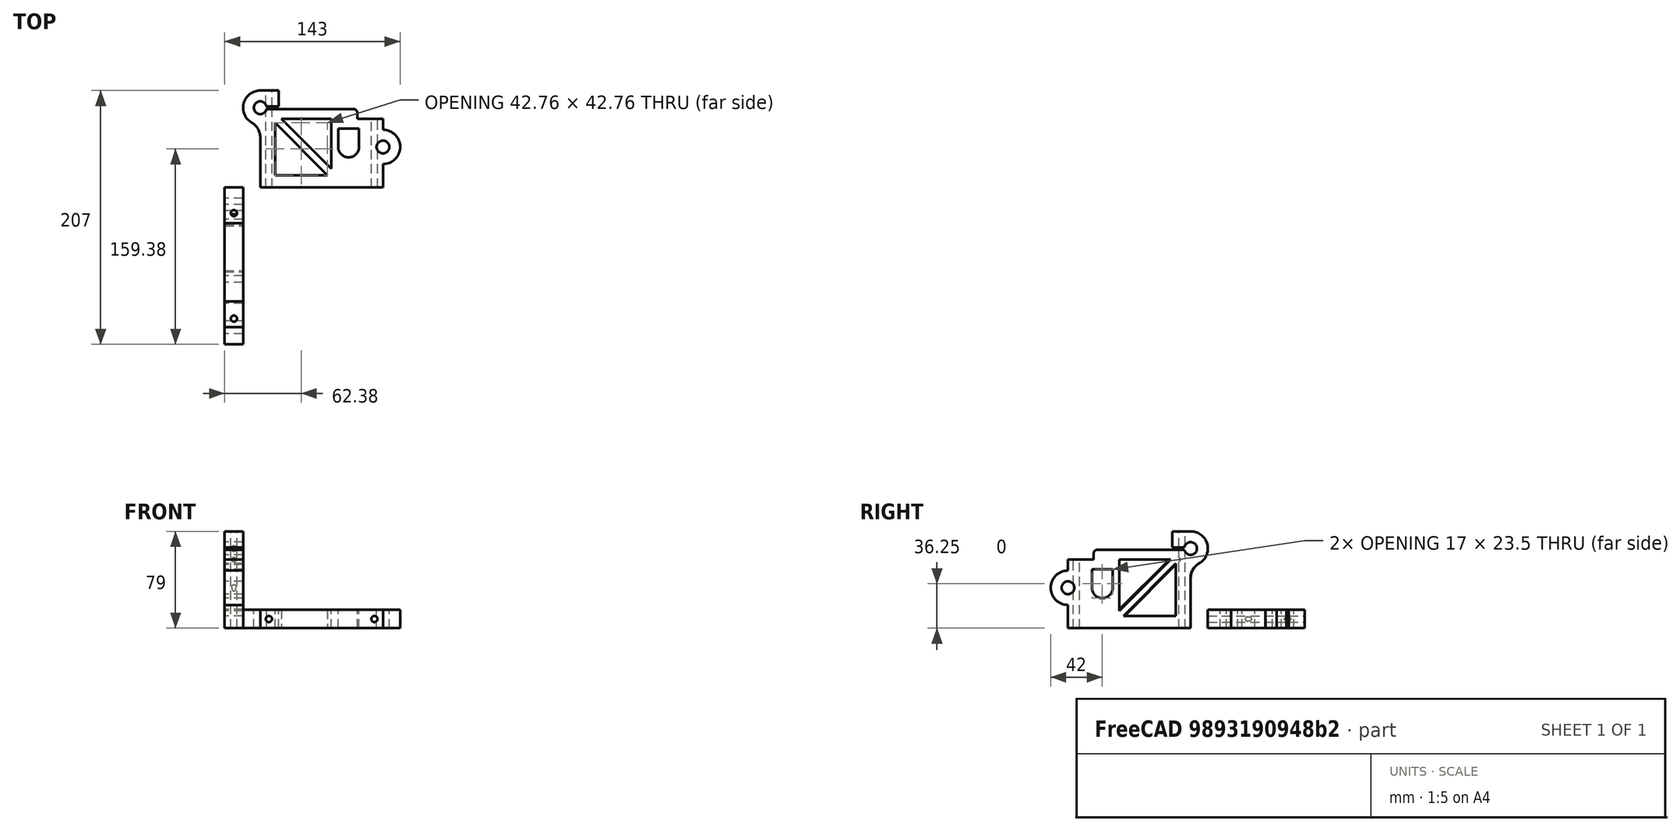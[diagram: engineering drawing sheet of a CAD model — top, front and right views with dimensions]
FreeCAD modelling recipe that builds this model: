
FCSTD DOCUMENT  (FreeCAD 0.15R4666 (Git))
Label: x_right_holder_B
License: All rights reserved
LicenseURL: http://en.wikipedia.org/wiki/All_rights_reserved
objects: Part::Box×7, Part::Cylinder×7, Part::MultiFuse×5, Part::Cut×5, Part::Feature×3, Part::Fillet×2, Mesh::Feature×1
note: 29 computed .brp shape members not serialized (recipe doc carries the construction recipe); baked Part::Feature solids carry a one-line shape summary decoded from their .brp

FEATURE [Part::Box] Box  label="Cubo"
  Height = 15
  Length = 100
  Placement = pos=(14,0,0) rot=(0,0,1;0rad)
  Width = 56
FEATURE [Part::Box] Box001  label="Cubo001"
  Height = 15
  Length = 15
  Placement = pos=(14,56,0) rot=(0,0,1;0rad)
  Width = 23
FEATURE [Part::Box] Box002  label="Cubo002"
  Height = 15
  Length = 64
  Placement = pos=(29,56,0) rot=(0,0,1;0rad)
  Width = 8
FEATURE [Part::Cylinder] Cylinder  label="Cilindro"
  Angle = 360
  Height = 15
  Placement = pos=(14,65,0) rot=(0,0,1;0rad)
  Radius = 14
FEATURE [Part::Cylinder] Cylinder001  label="Cilindro001"
  Angle = 360
  Height = 15
  Placement = pos=(114,33,0) rot=(0,0,1;0rad)
  Radius = 14
FEATURE [Part::Box] Box004  label="Cubo004"
  Height = 15
  Length = 46
  Placement = pos=(26,10,0) rot=(0,0,1;0rad)
  Width = 46
FEATURE [Part::Cylinder] Cylinder002  label="Cilindro002"
  Angle = 360
  Height = 17
  Placement = pos=(14,65,-1) rot=(0,0,1;0rad)
  Radius = 5.2
FEATURE [Part::Cylinder] Cylinder003  label="Cilindro003"
  Angle = 360
  Height = 17
  Placement = pos=(114,33,-1) rot=(0,0,1;0rad)
  Radius = 5.2
FEATURE [Part::MultiFuse] Fusion001  label="rod_holes"
  Shapes = -> [Cylinder002,Cylinder003]
FEATURE [Part::Box] Box006  label="Cubo006"
  Height = 15
  Length = 17
  Placement = pos=(77.5,33,0) rot=(0,0,1;0rad)
  Width = 15
FEATURE [Part::Cylinder] Cylinder004  label="Cilindro004"
  Angle = 360
  Height = 15
  Placement = pos=(86,33,0) rot=(0,0,1;0rad)
  Radius = 8.5
FEATURE [Part::MultiFuse] Fusion002  label="threaded_rod_hole"
  Shapes = -> [Box006,Cylinder004]
FEATURE [Part::Box] Box007  label="offset_hole"
  Height = 17
  Length = 12
  Placement = pos=(18,64,-1) rot=(0,0,1;0rad)
  Width = 2
FEATURE [Part::Cylinder] Cylinder005  label="Cilindro005"
  Angle = 360
  Height = 81
  Placement = pos=(21,-1,7.5) rot=(-1,0,0;1.5708rad)
  Radius = 2.5
FEATURE [Part::Cylinder] Cylinder006  label="Cilindro006"
  Angle = 360
  Height = 58
  Placement = pos=(107,-1,7.5) rot=(-1,0,0;1.5708rad)
  Radius = 2.5
FEATURE [Part::MultiFuse] Fusion004  label="vertical_holes"
  Shapes = -> [Cylinder005,Cylinder006]
FEATURE [Part::Box] Box009  label="Cubo009"
  Height = 15
  Length = 72
  Placement = pos=(23.76,55,0) rot=(0,0,-1;0.785398rad)
  Width = 6
FEATURE [Mesh::Feature] XholderRightoutside
FEATURE [Part::Feature] XholderRightoutside001001  label="XholderRightoutside002"
  shape: bbox 128 x 79.02 x 15 mm, 1051 faces, 0 solids (baked)
FEATURE [Part::MultiFuse] Fusion
  Shapes = -> [Box001,Cylinder001,Box,Box002,Cylinder]
FEATURE [Part::Cut] Cut
  Base = -> Fusion
  Tool = -> Box004
FEATURE [Part::Cut] Cut001
  Base = -> Cut
  Tool = -> Fusion002
FEATURE [Part::Cut] Cut002
  Base = -> Cut001
  Tool = -> Box007
FEATURE [Part::Cut] Cut003
  Base = -> Cut002
  Tool = -> Fusion001
FEATURE [Part::Cut] Cut004
  Base = -> Cut003
  Tool = -> Fusion004
FEATURE [Part::MultiFuse] Fusion005
  Shapes = -> [Cut004,Box009]
FEATURE [Part::Feature] Fillet001001  label="x_right_holder_B001"
  Placement = pos=(0,0,0) rot=(0.57735,-0.57735,-0.57735;2.0944rad)
  shape: bbox 15 x 128 x 79 mm, 33 faces (baked)
FEATURE [Part::Fillet] Fillet
  Base = -> Fusion005
  Edges = 1 edges r=14: [Edge11]
FEATURE [Part::Fillet] Fillet001002
  Base = -> Fillet
  Edges = 1 edges r=3: [Edge92]
FEATURE [Part::Feature] Fillet001002_solid  label="Fillet001002 (Solid)"
  Placement = pos=(0,0,0) rot=(0.57735,-0.57735,-0.57735;2.0944rad)
  shape: bbox 15 x 128 x 79 mm, 31 faces (baked)
